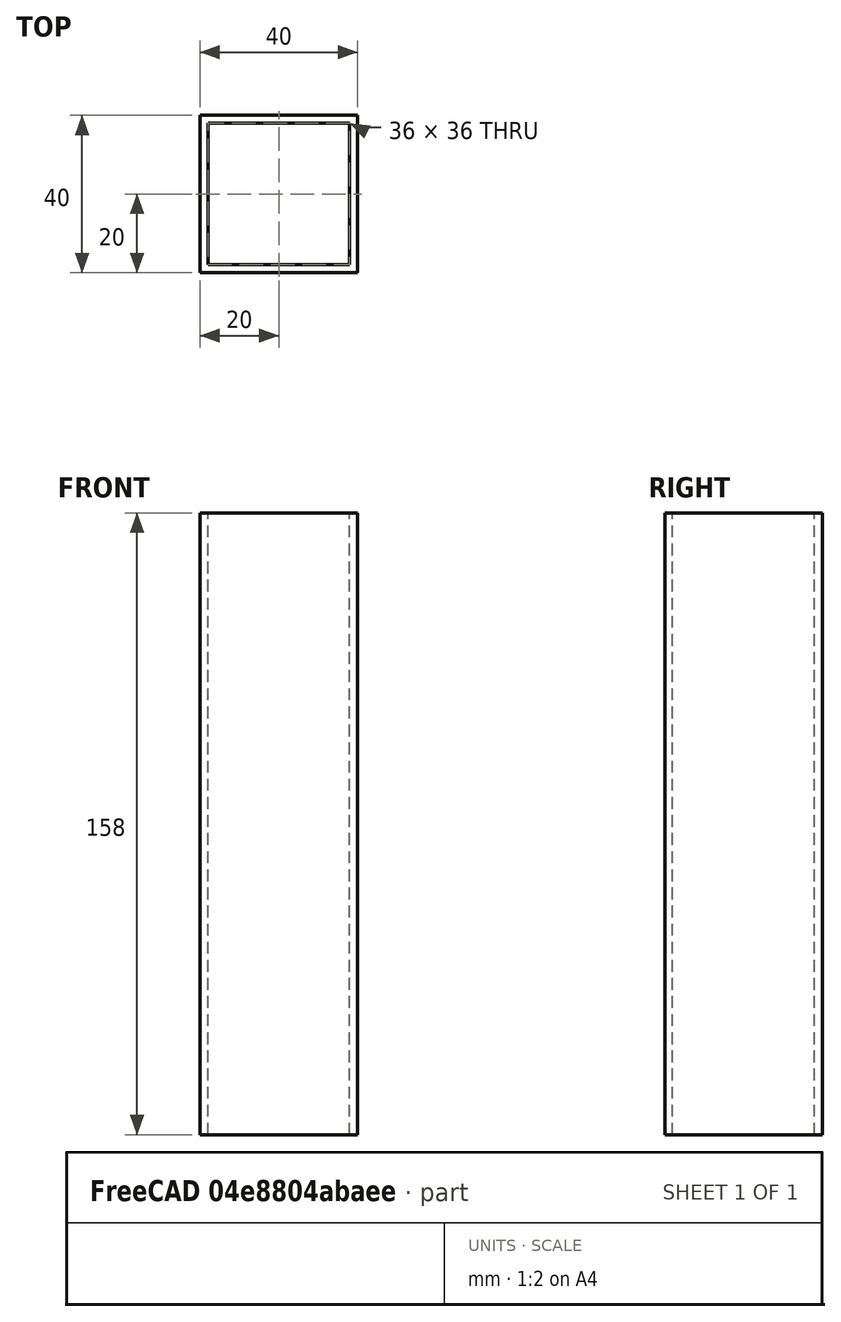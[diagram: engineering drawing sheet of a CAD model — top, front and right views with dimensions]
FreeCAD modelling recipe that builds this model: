
FCSTD DOCUMENT  (FreeCAD 0.21R33771 (Git))
Label: DistanzialeBasamentoC
License: All rights reserved
LicenseURL: http://en.wikipedia.org/wiki/All_rights_reserved
objects: Sketcher::SketchObject×1, PartDesign::Pad×1, PartDesign::CoordinateSystem×1, PartDesign::Body×1
note: 5 computed .brp shape members not serialized (recipe doc carries the construction recipe); baked Part::Feature solids carry a one-line shape summary decoded from their .brp

FEATURE [Sketcher::SketchObject] Sketch
  FullyConstrained = true
  MapMode = 5
  Support = -> [XY_Plane]
  sketch-geometry (8):
    g0: LineSegment StartX=0 StartY=0 StartZ=0 EndX=40 EndY=0 EndZ=0
    g1: LineSegment StartX=40 StartY=0 StartZ=0 EndX=40 EndY=40 EndZ=0
    g2: LineSegment StartX=40 StartY=40 StartZ=0 EndX=0 EndY=40 EndZ=0
    g3: LineSegment StartX=0 StartY=40 StartZ=0 EndX=0 EndY=0 EndZ=0
    g4: LineSegment StartX=2 StartY=38 StartZ=0 EndX=38 EndY=38 EndZ=0
    g5: LineSegment StartX=38 StartY=38 StartZ=0 EndX=38 EndY=2 EndZ=0
    g6: LineSegment StartX=38 StartY=2 StartZ=0 EndX=2 EndY=2 EndZ=0
    g7: LineSegment StartX=2 StartY=2 StartZ=0 EndX=2 EndY=38 EndZ=0
  constraints (23):
    c: Coincident(g0,g1)
    c: Coincident(g1,g2)
    c: Coincident(g2,g3)
    c: Coincident(g3,g0)
    c: Horizontal(g0)
    c: Horizontal(g2)
    c: Vertical(g1)
    c: Vertical(g3)
    c: Coincident(g0,g-1)
    c: DistanceX(g0,g0) = 40
    c: DistanceY(g3,g3) = 40
    c: Coincident(g4,g5)
    c: Coincident(g5,g6)
    c: Coincident(g6,g7)
    c: Coincident(g7,g4)
    c: Horizontal(g4)
    c: Horizontal(g6)
    c: Vertical(g5)
    c: Vertical(g7)
    c: DistanceX(g6,g6) = 36
    c: DistanceY(g5,g5) = 36
    c: DistanceX(g0,g6) = 2
    c: DistanceY(g0,g5) = 2
FEATURE [PartDesign::Pad] Pad
  Direction = (0,0,1)
  Length = 158
  Length2 = 10
  Profile = -> Sketch
  ReferenceAxis = -> Sketch [N_Axis]
  Type = 0
FEATURE [PartDesign::CoordinateSystem] LCS_DistanzialeBasamentoC
  AttacherType = Attacher::AttachEngine3D
FEATURE [PartDesign::Body] Body  label="Corpo"
  Group = -> [Sketch,Pad,LCS_DistanzialeBasamentoC]
  Origin = -> Origin
  Tip = -> Pad
